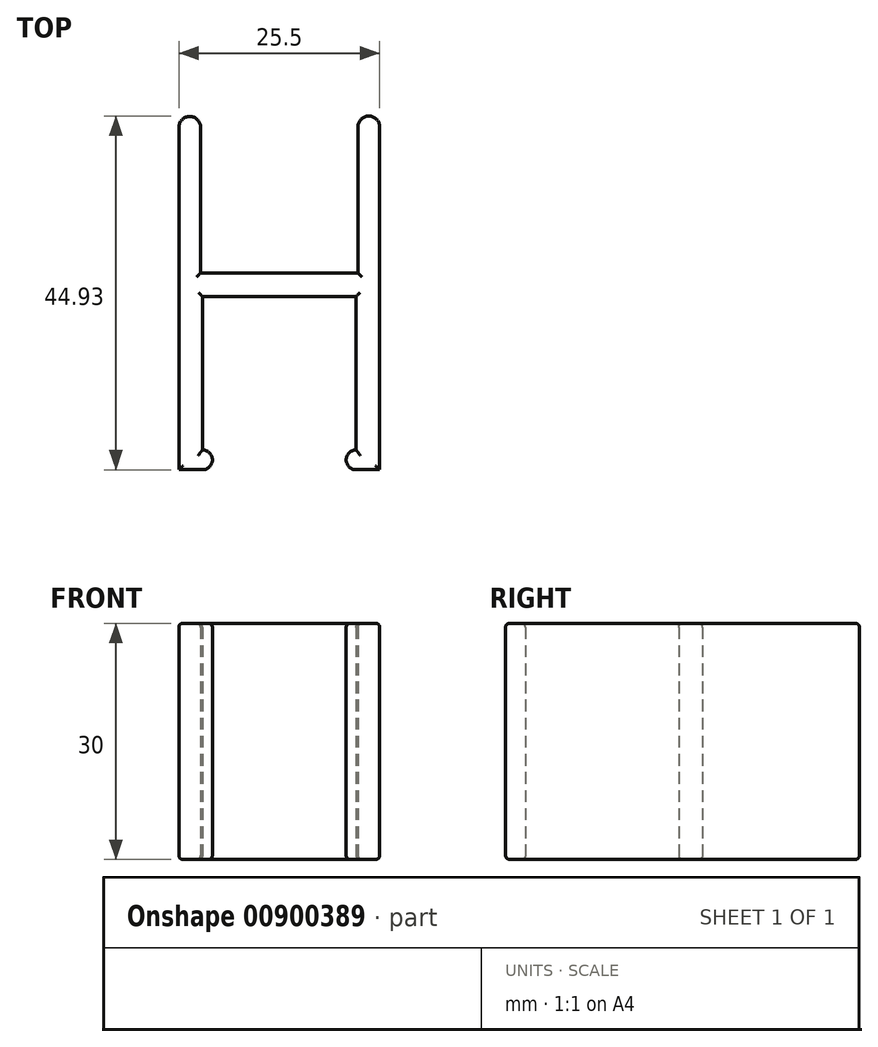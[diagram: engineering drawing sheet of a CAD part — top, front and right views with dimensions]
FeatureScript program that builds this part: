
annotation { "Feature Type Name" : "Feature", "Feature Type Description" : "" }
export const myFeature = defineFeature(function(context is Context, id is Id, definition is map)
    precondition{}
    {
        {
            var Q0;
            Q0=qCreatedBy(makeId("Top.planeOp"),FACE);
            var sketch = newSketch(context, id + "F0", { "sketchPlane" : qUnion([Q0])});
            skLineSegment(sketch, "E0", {"start": v(0, 0) * mm, "end": v(0, 30.2) * mm});
            skLineSegment(sketch, "E1", {"start": v(3, 8.7) * mm, "end": v(22.5, 8.7) * mm});
            skLineSegment(sketch, "E2", {"start": v(25.5, 30.26) * mm, "end": v(25.5, -13.3) * mm});
            skLineSegment(sketch, "E3", {"start": v(25.5, -13.3) * mm, "end": v(22.5, -13.3) * mm});
            skLineSegment(sketch, "E4", {"start": v(22.5, -13.3) * mm, "end": v(22.5, 8.7) * mm});
            skLineSegment(sketch, "E5", {"start": v(3, 8.7) * mm, "end": v(3, -13.3) * mm});
            skLineSegment(sketch, "E6", {"start": v(3, -13.3) * mm, "end": v(0, -13.3) * mm});
            skLineSegment(sketch, "E7", {"start": v(0, -13.3) * mm, "end": v(0, 0) * mm});
            skArc(sketch, "E8", {"start": v(3, -13.3) * mm, "mid": v(4.25, -12.05) * mm, "end": v(3, -10.8) * mm});
            skArc(sketch, "E9", {"start": v(22.5, -10.8) * mm, "mid": v(21.25, -12.05) * mm, "end": v(22.5, -13.3) * mm});
            skLineSegment(sketch, "E10", {"start": v(2.75, 11.7) * mm, "end": v(22.75, 11.7) * mm});
            skPoint(sketch, "E11.end.orphan", {"position": v(22.75, 30.26) * mm});
            skLineSegment(sketch, "E12", {"start": v(2.75, 11.7) * mm, "end": v(2.75, 30.2) * mm});
            skLineSegment(sketch, "E13", {"start": v(22.75, 11.7) * mm, "end": v(22.75, 30.26) * mm});
            skArc(sketch, "E14", {"start": v(2.75, 30.2) * mm, "mid": v(1.37, 31.58) * mm, "end": v(0, 30.2) * mm});
            skArc(sketch, "E15", {"start": v(25.5, 30.26) * mm, "mid": v(24.12, 31.63) * mm, "end": v(22.75, 30.26) * mm});
            skSolve(sketch);
        }
        {
            var Q0;
            Q0=makeQuery(id+"F0.imprint","IMPRINT",FACE,{"disambiguationData":[TD([[makeQuery(id+"F0.imprint","IMPRINT",EDGE,{"derivedFrom":sQuery(id+"F0.wireOp",EDGE,"E0")}),-1.0]])]});
            var Q1;
            {var subQ0=sQuery(id+"F0.wireOp",EDGE,"E8");Q1=makeQuery(id+"F0.imprint","IMPRINT",FACE,{"disambiguationData":[TD([[makeQuery(id+"F0.imprint","IMPRINT",EDGE,{"derivedFrom":subQ0}),1.0]])]});}
            var Q2;
            {var subQ0=sQuery(id+"F0.wireOp",EDGE,"E9");Q2=makeQuery(id+"F0.imprint","IMPRINT",FACE,{"disambiguationData":[TD([[makeQuery(id+"F0.imprint","IMPRINT",EDGE,{"derivedFrom":subQ0}),1.0]])]});}
            extrude(context, id + "F1", {"entities" : qUnion([Q0, Q1, Q2]), "depth" : 30 * mm, "offsetDistance" : 25 * mm});
        }
        {
            var Q0;
            Q0=makeQuery(id+"F1.opExtrude","CAP_EDGE",EDGE,{"disambiguationData":[OSD([sQuery(id+"F0.wireOp",EDGE,"E0"),sQuery(id+"F0.wireOp",EDGE,"E7")])],"isStart":false});
            var Q1;
            Q1=makeQuery(id+"F1.opExtrude","CAP_EDGE",EDGE,{"disambiguationData":[OSD([sQuery(id+"F0.wireOp",EDGE,"E5")])],"isStart":false});
            var Q2;
            Q2=makeQuery(id+"F1.opExtrude","CAP_EDGE",EDGE,{"disambiguationData":[OSD([sQuery(id+"F0.wireOp",EDGE,"E8")])],"isStart":false});
            var Q3;
            Q3=makeQuery(id+"F1.opExtrude","CAP_FACE",FACE,{"disambiguationData":[OSD([sQuery(id+"F0.wireOp",EDGE,"E0"),sQuery(id+"F0.wireOp",EDGE,"E1"),sQuery(id+"F0.wireOp",EDGE,"E2"),sQuery(id+"F0.wireOp",EDGE,"E3"),sQuery(id+"F0.wireOp",EDGE,"E4"),sQuery(id+"F0.wireOp",EDGE,"E5"),sQuery(id+"F0.wireOp",EDGE,"E6"),sQuery(id+"F0.wireOp",EDGE,"E7"),sQuery(id+"F0.wireOp",EDGE,"E8"),sQuery(id+"F0.wireOp",EDGE,"E9"),sQuery(id+"F0.wireOp",EDGE,"E10"),sQuery(id+"F0.wireOp",EDGE,"E12"),sQuery(id+"F0.wireOp",EDGE,"E13"),sQuery(id+"F0.wireOp",EDGE,"E14"),sQuery(id+"F0.wireOp",EDGE,"E15")])],"isStart":false});
            var Q4;
            Q4=makeQuery(id+"F1.opExtrude","CAP_FACE",FACE,{"disambiguationData":[OSD([sQuery(id+"F0.wireOp",EDGE,"E0"),sQuery(id+"F0.wireOp",EDGE,"E1"),sQuery(id+"F0.wireOp",EDGE,"E2"),sQuery(id+"F0.wireOp",EDGE,"E3"),sQuery(id+"F0.wireOp",EDGE,"E4"),sQuery(id+"F0.wireOp",EDGE,"E5"),sQuery(id+"F0.wireOp",EDGE,"E6"),sQuery(id+"F0.wireOp",EDGE,"E7"),sQuery(id+"F0.wireOp",EDGE,"E8"),sQuery(id+"F0.wireOp",EDGE,"E9"),sQuery(id+"F0.wireOp",EDGE,"E10"),sQuery(id+"F0.wireOp",EDGE,"E12"),sQuery(id+"F0.wireOp",EDGE,"E13"),sQuery(id+"F0.wireOp",EDGE,"E14"),sQuery(id+"F0.wireOp",EDGE,"E15")])],"isStart":true});
            fillet(context, id + "F2", {"entities" : qUnion([Q0, Q1, Q2, Q3, Q4]), "radius" : .5 * mm, "tangentPropagation" : true, "allowEdgeOverflow" : false});
        }
    });
